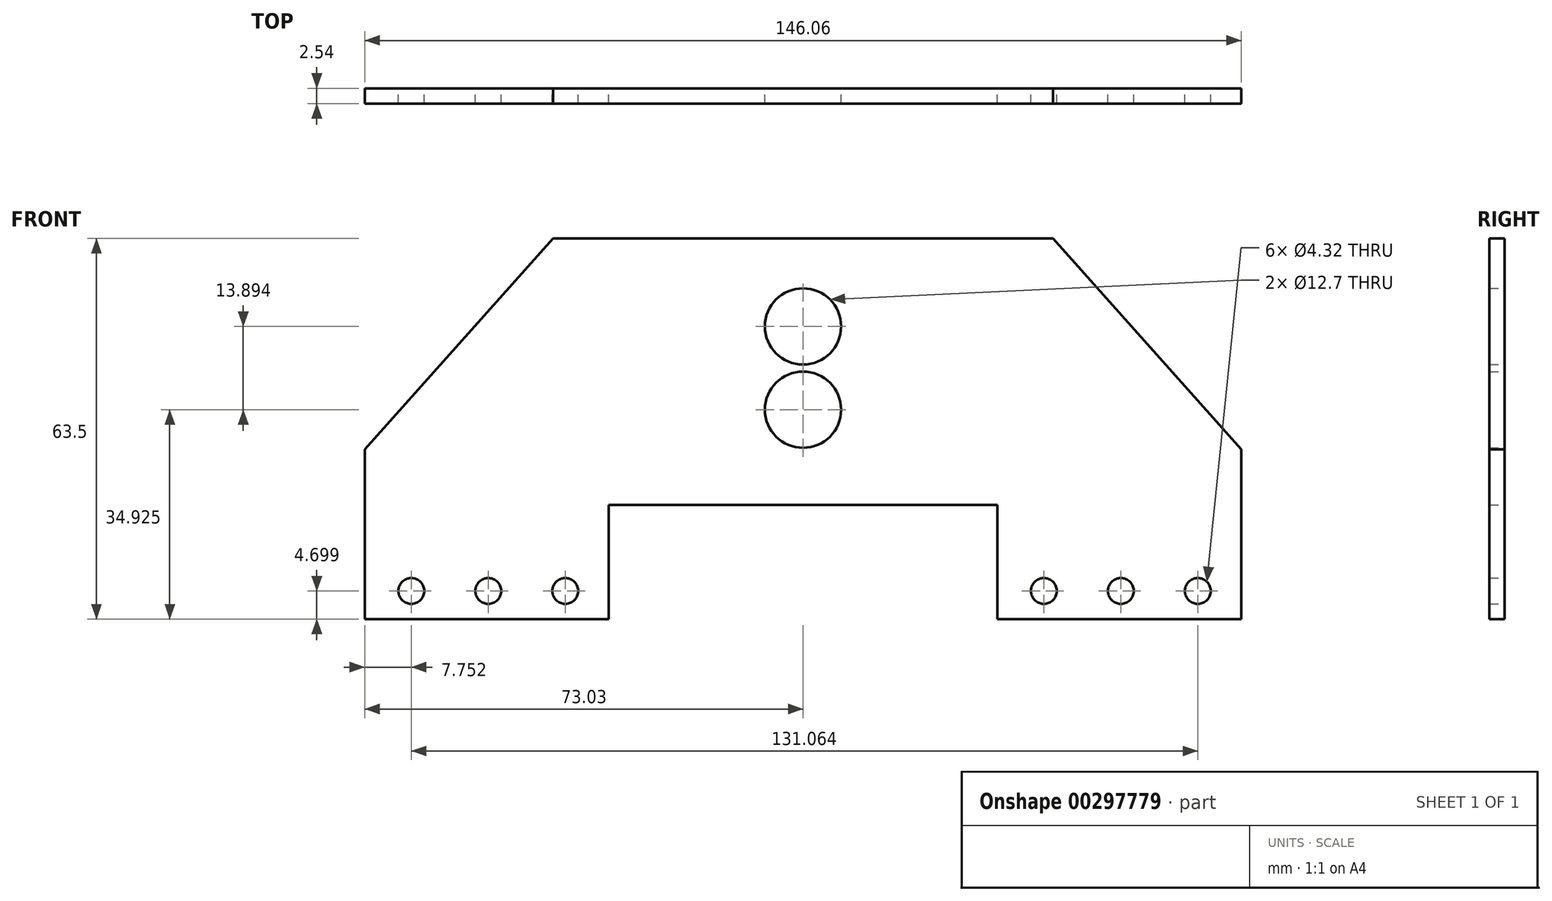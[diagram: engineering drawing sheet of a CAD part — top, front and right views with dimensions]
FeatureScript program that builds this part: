
annotation { "Feature Type Name" : "Feature", "Feature Type Description" : "" }
export const myFeature = defineFeature(function(context is Context, id is Id, definition is map)
    precondition{}
    {
        {
            var Q0;
            Q0=qCreatedBy(makeId("Front.planeOp"),FACE);
            var sketch = newSketch(context, id + "F0", { "sketchPlane" : qUnion([Q0])});
            skLineSegment(sketch, "E0.bottom", {"start": v(73.03, 31.75) * mm, "end": v(-73.03, 31.75) * mm});
            skLineSegment(sketch, "E0.top", {"start": v(73.03, -31.75) * mm, "end": v(-73.03, -31.75) * mm});
            skLineSegment(sketch, "E0.left", {"start": v(73.03, 31.75) * mm, "end": v(73.03, -31.75) * mm});
            skLineSegment(sketch, "E0.right", {"start": v(-73.03, 31.75) * mm, "end": v(-73.03, -31.75) * mm});
            skPoint(sketch, "E0.middle", {"position": v(0, 0) * mm});
            skLineSegment(sketch, "E1.bottom", {"start": v(-32.38, -31.75) * mm, "end": v(32.38, -31.75) * mm});
            skLineSegment(sketch, "E1.top", {"start": v(-32.38, -12.7) * mm, "end": v(32.38, -12.7) * mm});
            skLineSegment(sketch, "E1.left", {"start": v(-32.38, -31.75) * mm, "end": v(-32.38, -12.7) * mm});
            skLineSegment(sketch, "E1.right", {"start": v(32.38, -31.75) * mm, "end": v(32.38, -12.7) * mm});
            skLineSegment(sketch, "E2", {"start": v(32.38, -31.75) * mm, "end": v(73.03, -31.75) * mm});
            skLineSegment(sketch, "E3", {"start": v(-73.03, -31.75) * mm, "end": v(-32.38, -31.75) * mm});
            skLineSegment(sketch, "E4", {"start": v(-73.03, 31.75) * mm, "end": v(-32.39, 31.75) * mm});
            skLineSegment(sketch, "E5", {"start": v(73.03, 31.75) * mm, "end": v(32.38, 31.75) * mm});
            skLineSegment(sketch, "E6", {"start": v(-32.39, 31.75) * mm, "end": v(-41.66, 31.75) * mm});
            skLineSegment(sketch, "E7", {"start": v(32.38, 31.75) * mm, "end": v(41.66, 31.75) * mm});
            skLineSegment(sketch, "E8", {"start": v(-73.03, 31.75) * mm, "end": v(-73.03, -12.7) * mm});
            skLineSegment(sketch, "E9", {"start": v(73.03, 31.75) * mm, "end": v(73.03, -12.7) * mm});
            skLineSegment(sketch, "E10", {"start": v(-73.03, -12.7) * mm, "end": v(-73.03, -3.43) * mm});
            skLineSegment(sketch, "E11", {"start": v(73.03, -12.7) * mm, "end": v(73.03, -3.43) * mm});
            skLineSegment(sketch, "E12", {"start": v(-73.03, -3.43) * mm, "end": v(-41.66, 31.75) * mm});
            skLineSegment(sketch, "E13", {"start": v(41.66, 31.75) * mm, "end": v(73.03, -3.43) * mm});
            skCircle(sketch, "E14", {"center": v(0, 17.07) * mm, "radius": 6.35 * mm});
            skCircle(sketch, "E15", {"center": v(0, 3.18) * mm, "radius": 6.35 * mm});
            skCircle(sketch, "E16", {"center": v(-65.28, -27.05) * mm, "radius": 2.16 * mm});
            skCircle(sketch, "E17.1.0.0", {"center": v(-52.45, -27.05) * mm, "radius": 2.16 * mm});
            skCircle(sketch, "E17.2.0.0", {"center": v(-39.62, -27.05) * mm, "radius": 2.16 * mm});
            skLineSegment(sketch, "E17.direction1", {"start": v(-65.28, -27.05) * mm, "end": v(-52.45, -27.05) * mm, "construction": true});
            skCircle(sketch, "E18", {"center": v(40.13, -27.05) * mm, "radius": 2.16 * mm});
            skCircle(sketch, "E19.1.0.0", {"center": v(52.96, -27.05) * mm, "radius": 2.16 * mm});
            skCircle(sketch, "E19.2.0.0", {"center": v(65.79, -27.05) * mm, "radius": 2.16 * mm});
            skLineSegment(sketch, "E19.direction1", {"start": v(40.13, -27.05) * mm, "end": v(52.96, -27.05) * mm, "construction": true});
            skSolve(sketch);
        }
        {
            var Q0;
            Q0=makeQuery(id+"F0.imprint","IMPRINT",FACE,{"disambiguationData":[TD([[makeQuery(id+"F0.imprint","IMPRINT",EDGE,{"derivedFrom":sQuery(id+"F0.wireOp",EDGE,"E0.bottom")}),1.0]])]});
            extrude(context, id + "F1", {"entities" : qUnion([Q0]), "depth" : 2.54 * mm});
        }
    });
